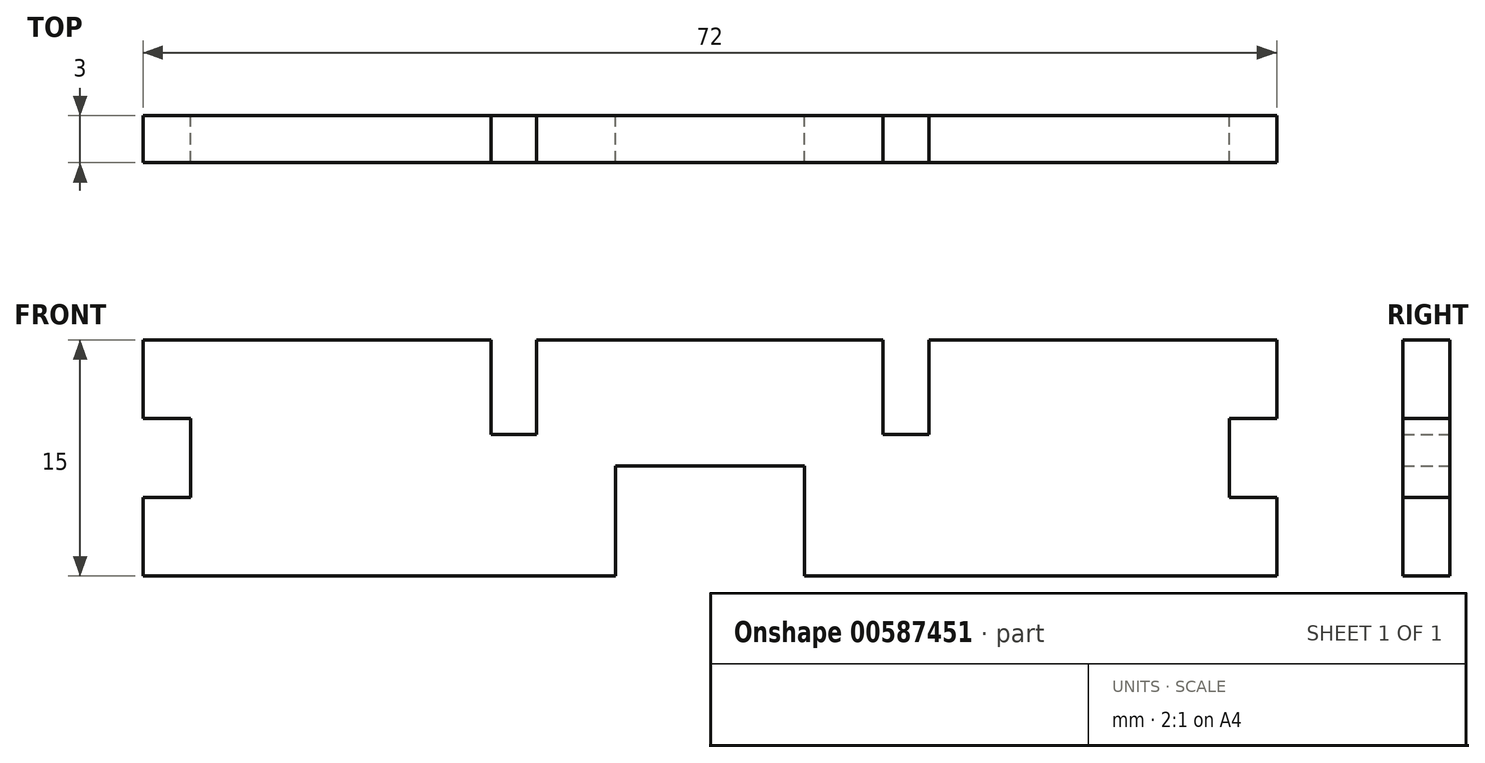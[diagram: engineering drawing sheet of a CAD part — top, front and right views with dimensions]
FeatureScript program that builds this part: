
annotation { "Feature Type Name" : "Feature", "Feature Type Description" : "" }
export const myFeature = defineFeature(function(context is Context, id is Id, definition is map)
    precondition{}
    {
        {
            var Q0;
            Q0=qCreatedBy(makeId("Front.planeOp"),FACE);
            var sketch = newSketch(context, id + "F0", { "sketchPlane" : qUnion([Q0])});
            skLineSegment(sketch, "E0", {"start": v(-36, 22.28) * mm, "end": v(-36, 17.28) * mm});
            skLineSegment(sketch, "E1", {"start": v(-36, 17.28) * mm, "end": v(-33, 17.28) * mm});
            skLineSegment(sketch, "E2", {"start": v(-33, 17.28) * mm, "end": v(-33, 12.28) * mm});
            skLineSegment(sketch, "E3", {"start": v(-33, 12.28) * mm, "end": v(-36, 12.28) * mm});
            skLineSegment(sketch, "E4", {"start": v(-36, 12.28) * mm, "end": v(-36, 7.28) * mm});
            skLineSegment(sketch, "E5", {"start": v(36, 22.28) * mm, "end": v(36, 17.28) * mm});
            skLineSegment(sketch, "E6", {"start": v(36, 17.28) * mm, "end": v(33, 17.28) * mm});
            skLineSegment(sketch, "E7", {"start": v(33, 17.28) * mm, "end": v(33, 12.28) * mm});
            skLineSegment(sketch, "E8", {"start": v(33, 12.28) * mm, "end": v(36, 12.28) * mm});
            skLineSegment(sketch, "E9", {"start": v(36, 12.28) * mm, "end": v(36, 7.28) * mm});
            skLineSegment(sketch, "E10", {"start": v(-36, 7.28) * mm, "end": v(-6, 7.28) * mm});
            skLineSegment(sketch, "E11", {"start": v(-6, 7.28) * mm, "end": v(-6, 14.28) * mm});
            skLineSegment(sketch, "E12", {"start": v(-6, 14.28) * mm, "end": v(6, 14.28) * mm});
            skLineSegment(sketch, "E13", {"start": v(6, 14.28) * mm, "end": v(6, 7.28) * mm});
            skLineSegment(sketch, "E14", {"start": v(6, 7.28) * mm, "end": v(36, 7.28) * mm});
            skLineSegment(sketch, "E15", {"start": v(11, 22.28) * mm, "end": v(11, 16.28) * mm});
            skLineSegment(sketch, "E16", {"start": v(11, 16.28) * mm, "end": v(13.9, 16.28) * mm});
            skLineSegment(sketch, "E17", {"start": v(13.9, 16.28) * mm, "end": v(13.9, 22.28) * mm});
            skLineSegment(sketch, "E18", {"start": v(13.9, 22.28) * mm, "end": v(36, 22.28) * mm});
            skLineSegment(sketch, "E19", {"start": v(-11, 22.28) * mm, "end": v(-11, 16.28) * mm});
            skLineSegment(sketch, "E20", {"start": v(-11, 16.28) * mm, "end": v(-13.9, 16.28) * mm});
            skLineSegment(sketch, "E21", {"start": v(-13.9, 16.28) * mm, "end": v(-13.9, 22.28) * mm});
            skLineSegment(sketch, "E22", {"start": v(-13.9, 22.28) * mm, "end": v(-36, 22.28) * mm});
            skLineSegment(sketch, "E23", {"start": v(-11, 22.28) * mm, "end": v(11, 22.28) * mm});
            skSolve(sketch);
        }
        {
            var Q0;
            Q0 = qSketchRegion(id + "F0", true);
            extrude(context, id + "F1", {"entities" : qUnion([Q0]), "depth" : 3 * mm, "offsetDistance" : 25 * mm});
        }
    });
